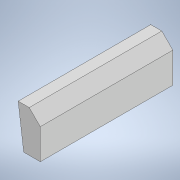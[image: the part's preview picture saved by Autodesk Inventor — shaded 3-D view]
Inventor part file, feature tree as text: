
AUTODESK INVENTOR PART (.ipt)
format: ipt  version: 2021 (Build 250183000, 183)  size: 185,344 bytes
history: native  units: in
note: dims shown in document units (in); Inventor stores cm internally (conversion verified against a paired STEP export)
features: extrude x8, sketch x8, projected_geometry x4
ambient origin geometry x8: Origin, YZ Plane, XZ Plane, XY Plane, X Axis, Y Axis, Z Axis, Center Point
bodies: Solid1 (feature_tree)
feature tree (20):
  extrude  "Extrusion1"  Depth=0.2362in
  extrude  "Extrusion2"  Depth=0.5906in
  extrude  "Extrusion3"  Depth=0.3937in TaperAngle=0.0deg
  extrude  "Extrusion4"  Depth=1.1024in TaperAngle=0.0deg
  extrude  "Extrusion5"  Depth=0.5906in
  extrude  "Extrusion6"  Depth=1.3312in TaperAngle=0.0deg
  extrude  "Extrusion7"  Depth=1.1811in TaperAngle=0.0deg
  extrude  "Extrusion8"  Depth=0.6939in TaperAngle=0.0deg
  sketch  "Sketch1"  dims[d0=0.2362in d1=0.4331in]
  sketch  "Sketch2"  dims[d2=0.5906in d4=0.0787in]
  sketch  "Sketch3"  dims[d5=0.0787in d6=0.3937in d7=0.0in]
  projected_geometry  "Projected Loop1"
  sketch  "Sketch6"  dims[d9=0.1181in d12=1.1024in d13=0.0in]
  sketch  "Sketch7"  dims[d14=0.3937in d15=0.0in d19=0.5906in]
  projected_geometry  "Projected Loop3"
  sketch  "Sketch8"  dims[d20=0.0787in d21=1.3312in d22=0.0in]
  projected_geometry  "Projected Loop4"
  sketch  "Sketch10"  dims[d23=1.3312in d24=0.0in d25=1.1811in d26=0.0787in d27=0.0in d28=0.0in]
  sketch  "Sketch12"  dims[d29=0.3937in d31=0.6939in d32=0.0in d33=0.0787in d34=0.6939in d35=0.0in d36=0.0157in]
  projected_geometry  "Projected Loop6"
